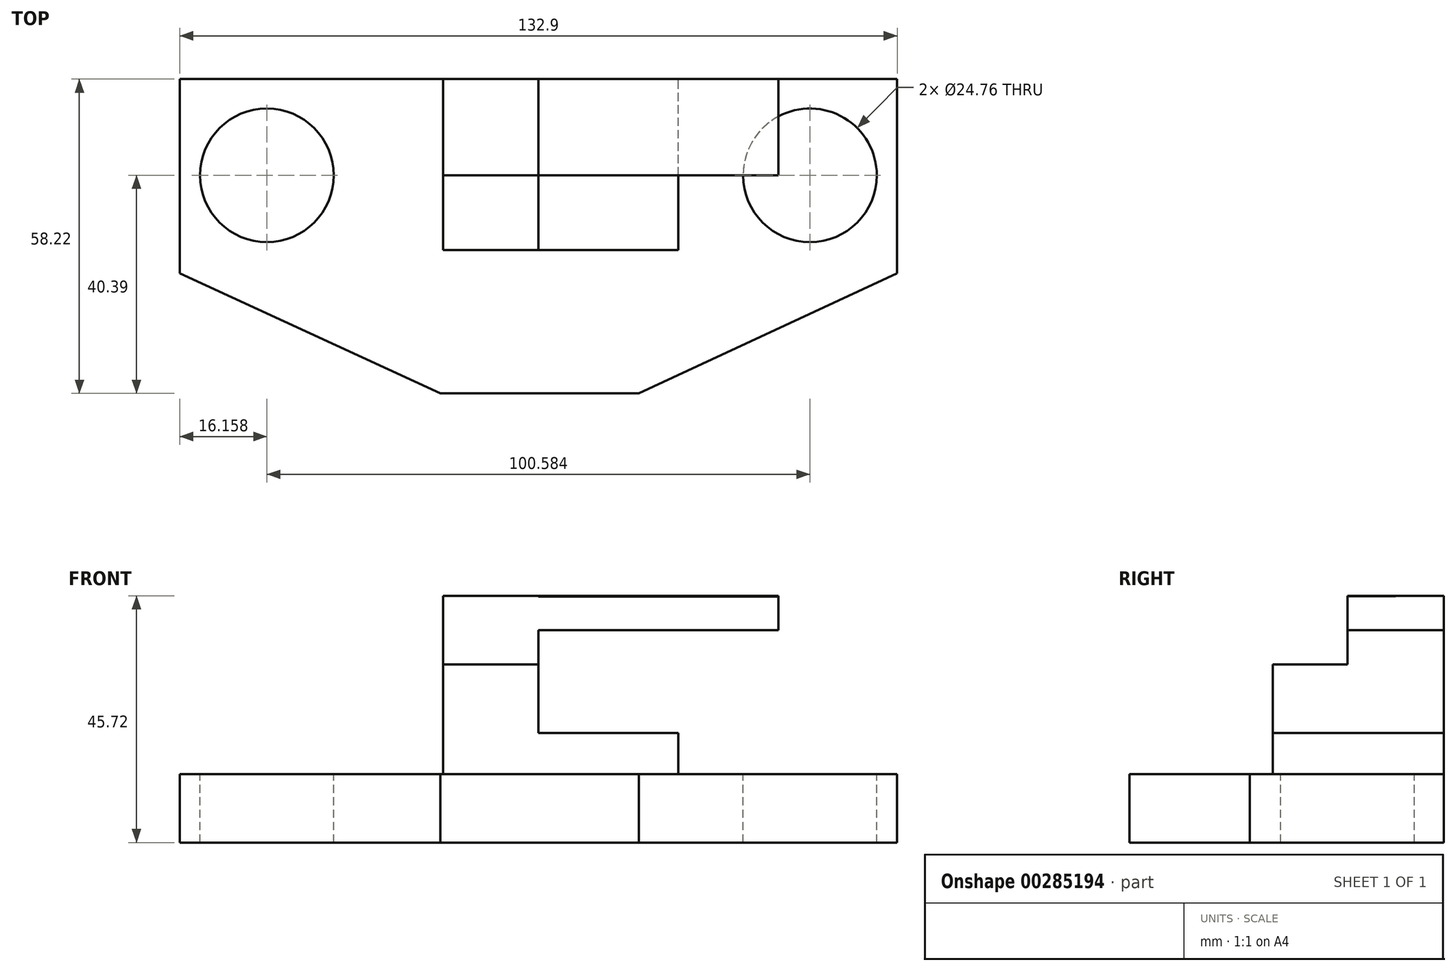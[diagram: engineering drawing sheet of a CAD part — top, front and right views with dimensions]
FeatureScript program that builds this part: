
annotation { "Feature Type Name" : "Feature", "Feature Type Description" : "" }
export const myFeature = defineFeature(function(context is Context, id is Id, definition is map)
    precondition{}
    {
        {
            var Q0;
            Q0=qCreatedBy(makeId("Top.planeOp"),FACE);
            var sketch = newSketch(context, id + "F0", { "sketchPlane" : qUnion([Q0])});
            skLineSegment(sketch, "E0", {"start": v(-18.18, -40.39) * mm, "end": v(18.6, -40.39) * mm});
            skLineSegment(sketch, "E1", {"start": v(18.6, -40.39) * mm, "end": v(66.45, -18.14) * mm});
            skLineSegment(sketch, "E2", {"start": v(66.45, -18.14) * mm, "end": v(66.45, 17.83) * mm});
            skLineSegment(sketch, "E3", {"start": v(-18.18, -40.39) * mm, "end": v(-66.45, -18.14) * mm});
            skLineSegment(sketch, "E4", {"start": v(-66.45, -18.14) * mm, "end": v(-66.45, 17.83) * mm});
            skLineSegment(sketch, "E5", {"start": v(-66.45, 17.83) * mm, "end": v(66.45, 17.83) * mm});
            skSolve(sketch);
        }
        {
            var Q0;
            Q0=makeQuery(id+"F0.imprint","IMPRINT",FACE,{"disambiguationData":[TD([[makeQuery(id+"F0.imprint","IMPRINT",EDGE,{"derivedFrom":sQuery(id+"F0.wireOp",EDGE,"E0")}),1.0]])]});
            extrude(context, id + "F1", {"entities" : qUnion([Q0]), "depth" : 12.7 * mm});
        }
        {
            var Q0;
            Q0=makeQuery(id+"F1.opExtrude","CAP_FACE",FACE,{"disambiguationData":[OSD([sQuery(id+"F0.wireOp",EDGE,"E0"),sQuery(id+"F0.wireOp",EDGE,"E1"),sQuery(id+"F0.wireOp",EDGE,"E2"),sQuery(id+"F0.wireOp",EDGE,"E3"),sQuery(id+"F0.wireOp",EDGE,"E4"),sQuery(id+"F0.wireOp",EDGE,"E5")])],"isStart":false});
            var sketch = newSketch(context, id + "F2", { "sketchPlane" : qUnion([Q0])});
            skCircle(sketch, "E6", {"center": v(50.3, 0) * mm, "radius": 12.38 * mm});
            skCircle(sketch, "E7", {"center": v(-50.3, 0) * mm, "radius": 12.38 * mm});
            skSolve(sketch);
        }
        {
            var Q0;
            Q0=makeQuery(id+"F2.imprint","IMPRINT",FACE,{"disambiguationData":[TD([[makeQuery(id+"F2.imprint","IMPRINT",EDGE,{"derivedFrom":sQuery(id+"F2.wireOp",EDGE,"E6")}),1.0]])]});
            var Q1;
            Q1=makeQuery(id+"F2.imprint","IMPRINT",FACE,{"disambiguationData":[TD([[makeQuery(id+"F2.imprint","IMPRINT",EDGE,{"derivedFrom":sQuery(id+"F2.wireOp",EDGE,"E7")}),1.0]])]});
            extrude(context, id + "F3", {"entities" : qUnion([Q0, Q1]), "operationType" : NewBodyOperationType.REMOVE, "oppositeDirection" : true, "depth" : 25.4 * mm});
        }
        {
            var Q0;
            Q0=makeQuery(id+"F1.opExtrude","CAP_FACE",FACE,{"disambiguationData":[OSD([sQuery(id+"F0.wireOp",EDGE,"E0"),sQuery(id+"F0.wireOp",EDGE,"E1"),sQuery(id+"F0.wireOp",EDGE,"E2"),sQuery(id+"F0.wireOp",EDGE,"E3"),sQuery(id+"F0.wireOp",EDGE,"E4"),sQuery(id+"F0.wireOp",EDGE,"E5")])],"isStart":false});
            var sketch = newSketch(context, id + "F4", { "sketchPlane" : qUnion([Q0])});
            skLineSegment(sketch, "E8", {"start": v(-17.68, 17.83) * mm, "end": v(-17.68, -13.87) * mm});
            skLineSegment(sketch, "E9", {"start": v(-17.68, -13.87) * mm, "end": v(25.9, -13.87) * mm});
            skLineSegment(sketch, "E10", {"start": v(25.9, -13.87) * mm, "end": v(25.9, 17.83) * mm});
            skLineSegment(sketch, "E11", {"start": v(25.9, 17.83) * mm, "end": v(-17.68, 17.83) * mm});
            skSolve(sketch);
        }
        {
            var Q0;
            Q0=makeQuery(id+"F4.imprint","IMPRINT",FACE,{"disambiguationData":[TD([[makeQuery(id+"F4.imprint","IMPRINT",EDGE,{"derivedFrom":sQuery(id+"F4.wireOp",EDGE,"E8")}),1.0]])]});
            extrude(context, id + "F5", {"entities" : qUnion([Q0]), "operationType" : NewBodyOperationType.ADD, "depth" : 7.62 * mm});
        }
        {
            var Q0;
            Q0=makeQuery(id+"F5.opExtrude","CAP_FACE",FACE,{"disambiguationData":[OSD([sQuery(id+"F4.wireOp",EDGE,"E8"),sQuery(id+"F4.wireOp",EDGE,"E9"),sQuery(id+"F4.wireOp",EDGE,"E10"),sQuery(id+"F4.wireOp",EDGE,"E11")])],"isStart":false});
            var sketch = newSketch(context, id + "F6", { "sketchPlane" : qUnion([Q0])});
            skLineSegment(sketch, "E12", {"start": v(0, 17.83) * mm, "end": v(0, -13.87) * mm});
            skLineSegment(sketch, "E13", {"start": v(0, 0) * mm, "end": v(-17.68, 0) * mm});
            skSolve(sketch);
        }
        {
            var Q0;
            Q0 = qSketchRegion(id + "F6", true);
            var Q1;
            {var subQ3=sQuery(id+"F6.wireOp",EDGE,"E13");Q1=makeQuery(id+"F6.imprint","IMPRINT",FACE,{"disambiguationData":[TD([[makeQuery(id+"F6.imprint","IMPRINT",EDGE,{"derivedFrom":subQ3}),1.0]])]});}
            extrude(context, id + "F7", {"entities" : qUnion([Q0, Q1]), "operationType" : NewBodyOperationType.ADD, "depth" : 12.7 * mm});
        }
        {
            var Q0;
            Q0=makeQuery(id+"F5.opExtrude","CAP_FACE",FACE,{"disambiguationData":[OSD([sQuery(id+"F4.wireOp",EDGE,"E8"),sQuery(id+"F4.wireOp",EDGE,"E9"),sQuery(id+"F4.wireOp",EDGE,"E10"),sQuery(id+"F4.wireOp",EDGE,"E11")])],"isStart":false});
            var sketch = newSketch(context, id + "F8", { "sketchPlane" : qUnion([Q0])});
            skLineSegment(sketch, "E14", {"start": v(0, 0) * mm, "end": v(0, 17.83) * mm});
            skLineSegment(sketch, "E15", {"start": v(0, 17.83) * mm, "end": v(-17.68, 17.83) * mm});
            skLineSegment(sketch, "E16", {"start": v(-17.68, 17.83) * mm, "end": v(-17.68, 0) * mm});
            skLineSegment(sketch, "E17", {"start": v(-17.68, 0) * mm, "end": v(0, 0) * mm});
            skSolve(sketch);
        }
        {
            var Q0;
            Q0 = qSketchRegion(id + "F8", true);
            extrude(context, id + "F9", {"entities" : qUnion([Q0]), "operationType" : NewBodyOperationType.ADD, "depth" : 25.4 * mm});
        }
        {
            var Q0;
            Q0=makeQuery(id+"F9.boolean.opBoolean","MERGE",FACE,{"derivedFrom":[makeQuery(id+"F7.opExtrude","SWEPT_FACE",FACE,{"disambiguationData":[OSD([sQuery(id+"F6.wireOp",EDGE,"E12")])]}),makeQuery(id+"F9.opExtrude","SWEPT_FACE",FACE,{"disambiguationData":[OSD([sQuery(id+"F8.wireOp",EDGE,"E14")])]})]});
            var sketch = newSketch(context, id + "F10", { "sketchPlane" : qUnion([Q0])});
            skLineSegment(sketch, "E18", {"start": v(0, 39.37) * mm, "end": v(17.83, 39.37) * mm});
            skLineSegment(sketch, "E19", {"start": v(17.83, 39.37) * mm, "end": v(17.83, 45.72) * mm});
            skLineSegment(sketch, "E20", {"start": v(17.83, 45.72) * mm, "end": v(0, 45.57) * mm});
            skLineSegment(sketch, "E21", {"start": v(0, 45.57) * mm, "end": v(0, 39.37) * mm});
            skSolve(sketch);
        }
        {
            var Q0;
            Q0=makeQuery(id+"F10.imprint","IMPRINT",FACE,{"disambiguationData":[TD([[makeQuery(id+"F10.imprint","IMPRINT",EDGE,{"derivedFrom":sQuery(id+"F10.wireOp",EDGE,"E18")}),1.0]])]});
            extrude(context, id + "F11", {"entities" : qUnion([Q0]), "operationType" : NewBodyOperationType.ADD, "depth" : 44.45 * mm});
        }
    });
